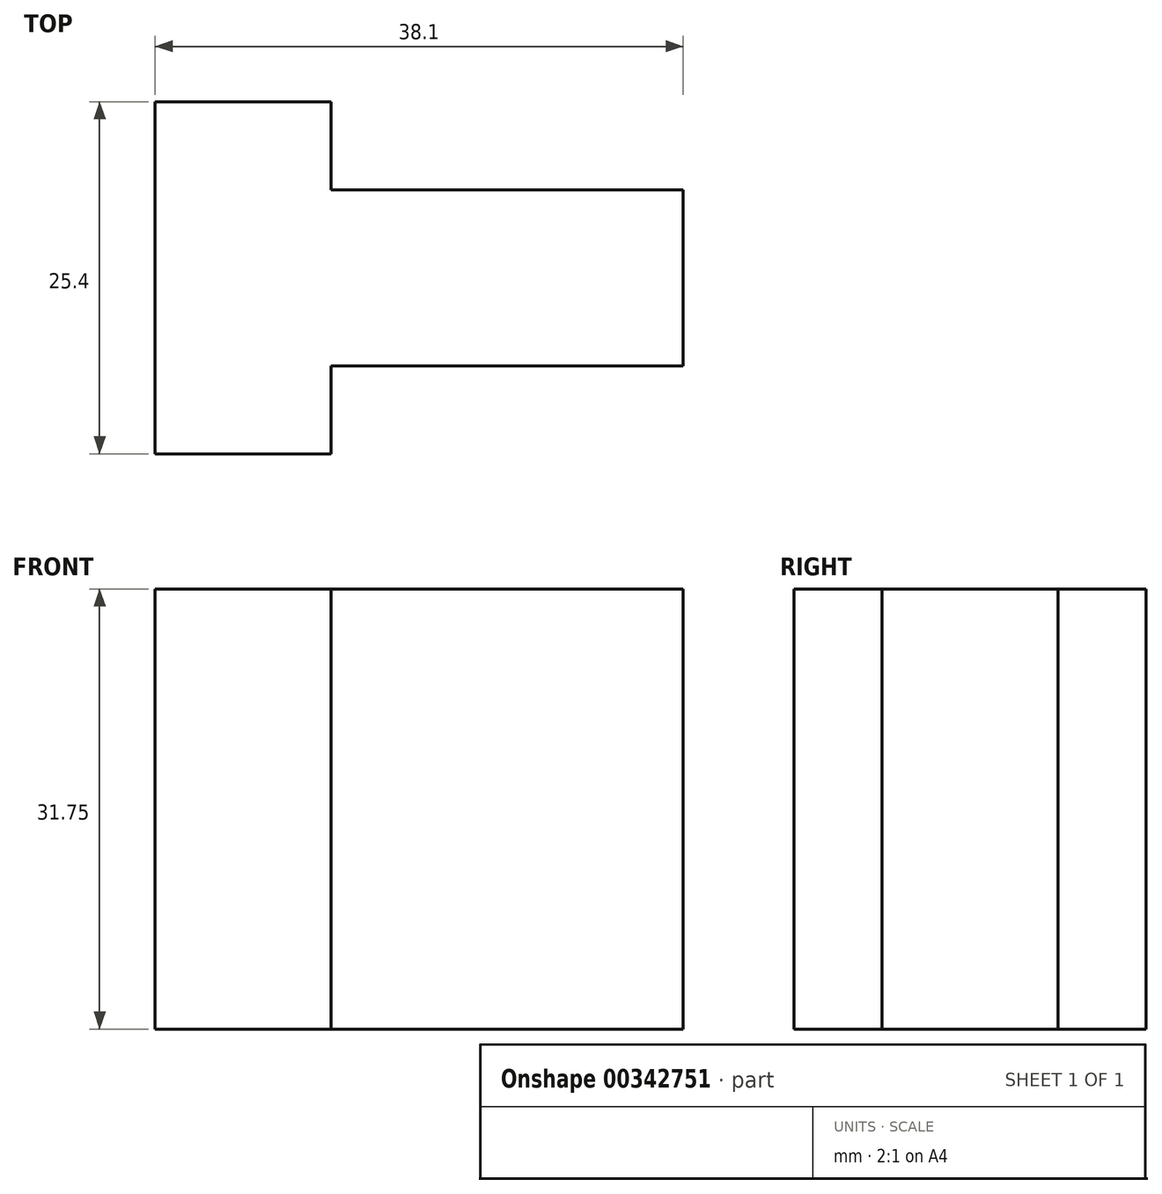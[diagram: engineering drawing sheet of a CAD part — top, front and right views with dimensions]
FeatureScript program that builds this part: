
annotation { "Feature Type Name" : "Feature", "Feature Type Description" : "" }
export const myFeature = defineFeature(function(context is Context, id is Id, definition is map)
    precondition{}
    {
        {
            var Q0;
            Q0=qCreatedBy(makeId("Top.planeOp"),FACE);
            var sketch = newSketch(context, id + "F0", { "sketchPlane" : qUnion([Q0])});
            skLineSegment(sketch, "E0", {"start": v(0, 0) * mm, "end": v(0, 25.4) * mm});
            skLineSegment(sketch, "E1", {"start": v(0, 25.4) * mm, "end": v(12.7, 25.4) * mm});
            skLineSegment(sketch, "E2", {"start": v(12.7, 25.4) * mm, "end": v(12.7, 19.05) * mm});
            skLineSegment(sketch, "E3", {"start": v(12.7, 19.05) * mm, "end": v(38.1, 19.05) * mm});
            skLineSegment(sketch, "E4", {"start": v(38.1, 19.05) * mm, "end": v(38.1, 6.35) * mm});
            skLineSegment(sketch, "E5", {"start": v(38.1, 6.35) * mm, "end": v(12.7, 6.35) * mm});
            skLineSegment(sketch, "E6", {"start": v(12.7, 6.35) * mm, "end": v(12.7, 0) * mm});
            skLineSegment(sketch, "E7", {"start": v(12.7, 0) * mm, "end": v(0, 0) * mm});
            skSolve(sketch);
        }
        {
            var Q0;
            Q0 = qSketchRegion(id + "F0", true);
            extrude(context, id + "F1", {"entities" : qUnion([Q0]), "depth" : 31.75 * mm});
        }
    });
